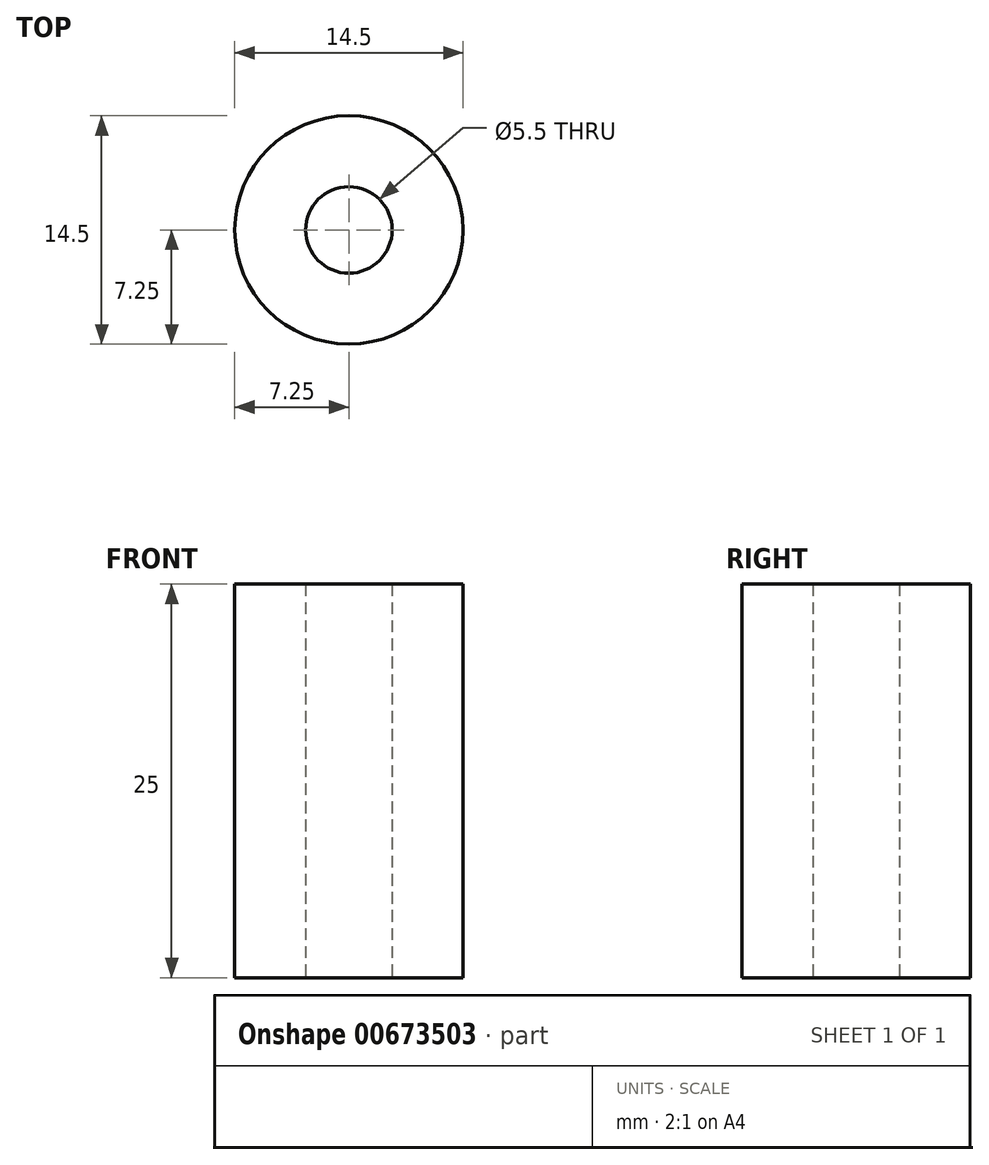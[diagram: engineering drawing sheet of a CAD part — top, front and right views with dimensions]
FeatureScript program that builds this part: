
annotation { "Feature Type Name" : "Feature", "Feature Type Description" : "" }
export const myFeature = defineFeature(function(context is Context, id is Id, definition is map)
    precondition{}
    {
        {
            var Q0;
            Q0=qCreatedBy(makeId("Top.planeOp"),FACE);
            var sketch = newSketch(context, id + "F0", { "sketchPlane" : qUnion([Q0])});
            skCircle(sketch, "E0", {"center": v(0, 0) * mm, "radius": 2.75 * mm});
            skCircle(sketch, "E1", {"center": v(0, 0) * mm, "radius": 7.25 * mm});
            skSolve(sketch);
        }
        {
            var Q0;
            Q0 = qSketchRegion(id + "F0", true);
            extrude(context, id + "F1", {"entities" : qUnion([Q0]), "depth" : 25 * mm, "offsetDistance" : 25 * mm});
        }
    });
